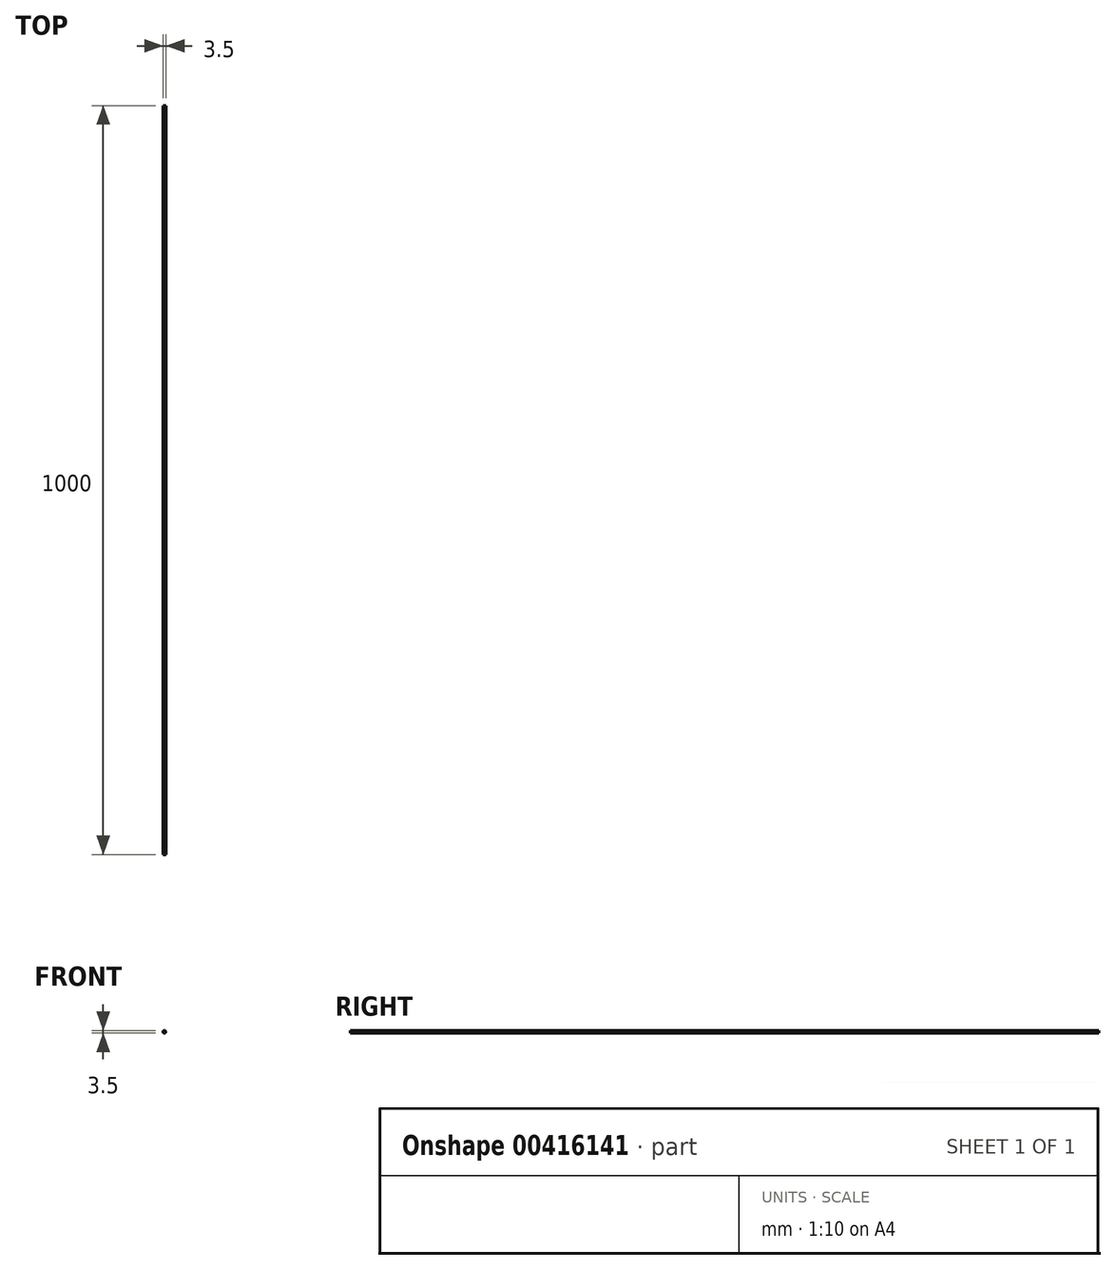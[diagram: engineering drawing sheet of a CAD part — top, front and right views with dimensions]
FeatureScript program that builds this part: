
annotation { "Feature Type Name" : "Feature", "Feature Type Description" : "" }
export const myFeature = defineFeature(function(context is Context, id is Id, definition is map)
    precondition{}
    {
        {
            var Q0;
            Q0=qCreatedBy(makeId("Front.planeOp"),FACE);
            var sketch = newSketch(context, id + "F0", { "sketchPlane" : qUnion([Q0])});
            skCircle(sketch, "E0", {"center": v(0, 0) * mm, "radius": 1.75 * mm});
            skSolve(sketch);
        }
        {
            var Q0;
            Q0=makeQuery(id+"F0.imprint","IMPRINT",FACE,{"disambiguationData":[TD([[makeQuery(id+"F0.imprint","IMPRINT",EDGE,{"derivedFrom":sQuery(id+"F0.wireOp",EDGE,"E0")}),1.0]])]});
            extrude(context, id + "F1", {"entities" : qUnion([Q0]), "depth" : 1000 * mm, "offsetDistance" : 25 * mm});
        }
    });
